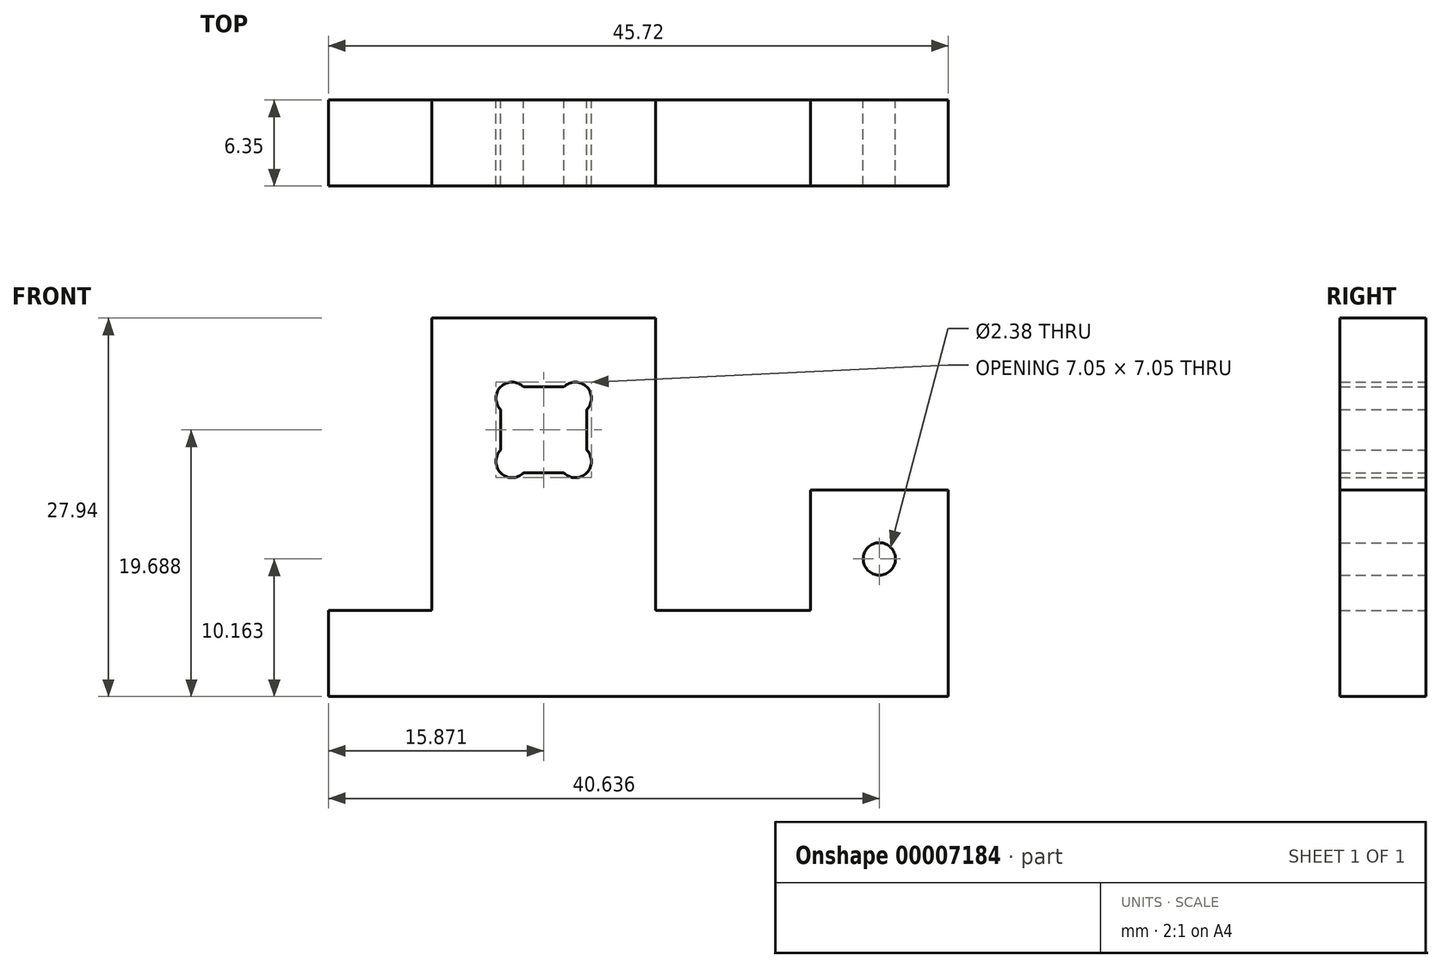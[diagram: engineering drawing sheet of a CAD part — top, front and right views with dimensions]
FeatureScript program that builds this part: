
annotation { "Feature Type Name" : "Feature", "Feature Type Description" : "" }
export const myFeature = defineFeature(function(context is Context, id is Id, definition is map)
    precondition{}
    {
        {
            var Q0;
            Q0=qCreatedBy(makeId("Front.planeOp"),FACE);
            var sketch = newSketch(context, id + "F0", { "sketchPlane" : qUnion([Q0])});
            skLineSegment(sketch, "E0", {"start": v(-37.65, 9.84) * mm, "end": v(-37.65, -11.75) * mm});
            skLineSegment(sketch, "E1", {"start": v(-37.65, -18.1) * mm, "end": v(0.45, -18.1) * mm});
            skLineSegment(sketch, "E2", {"start": v(0.45, -2.86) * mm, "end": v(-9.71, -2.86) * mm});
            skLineSegment(sketch, "E3", {"start": v(-9.71, -2.86) * mm, "end": v(-9.71, -11.75) * mm});
            skLineSegment(sketch, "E4", {"start": v(-9.71, -11.75) * mm, "end": v(-21.14, -11.75) * mm});
            skLineSegment(sketch, "E5", {"start": v(-21.14, -11.75) * mm, "end": v(-21.14, 9.84) * mm});
            skLineSegment(sketch, "E6", {"start": v(-21.14, 9.84) * mm, "end": v(-37.65, 9.84) * mm});
            skLineSegment(sketch, "E7.bottom", {"start": v(-30.9, 4.76) * mm, "end": v(-27.9, 4.76) * mm});
            skLineSegment(sketch, "E7.top", {"start": v(-30.9, -1.59) * mm, "end": v(-27.9, -1.59) * mm});
            skLineSegment(sketch, "E7.left", {"start": v(-32.57, 3.08) * mm, "end": v(-32.57, 0.1) * mm});
            skLineSegment(sketch, "E7.right", {"start": v(-26.22, 3.08) * mm, "end": v(-26.22, 0.1) * mm});
            skPoint(sketch, "E8", {"position": v(-4.63, -2.86) * mm});
            skCircle(sketch, "E9", {"center": v(-4.63, -7.94) * mm, "radius": 1.2 * mm});
            skLineSegment(sketch, "E10", {"start": v(0.45, -2.86) * mm, "end": v(0.45, -18.1) * mm});
            skLineSegment(sketch, "E11.bottom", {"start": v(-37.65, -11.75) * mm, "end": v(-45.27, -11.75) * mm});
            skLineSegment(sketch, "E11.top", {"start": v(-37.65, -18.1) * mm, "end": v(-45.27, -18.1) * mm});
            skLineSegment(sketch, "E11.right", {"start": v(-45.27, -11.75) * mm, "end": v(-45.27, -18.1) * mm});
            skLineSegment(sketch, "E12", {"start": v(-32.57, 4.76) * mm, "end": v(-26.22, -1.59) * mm, "construction": true});
            skLineSegment(sketch, "E13", {"start": v(-26.22, 4.76) * mm, "end": v(-32.57, -1.59) * mm, "construction": true});
            skArc(sketch, "E14", {"start": v(-30.9, 4.76) * mm, "mid": v(-32.57, 4.76) * mm, "end": v(-32.57, 3.08) * mm});
            skArc(sketch, "E15", {"start": v(-26.22, 3.08) * mm, "mid": v(-26.22, 4.76) * mm, "end": v(-27.9, 4.76) * mm});
            skArc(sketch, "E16", {"start": v(-27.9, -1.59) * mm, "mid": v(-26.22, -1.59) * mm, "end": v(-26.22, 0.1) * mm});
            skArc(sketch, "E17", {"start": v(-32.57, 0.1) * mm, "mid": v(-32.57, -1.59) * mm, "end": v(-30.9, -1.59) * mm});
            skSolve(sketch);
        }
        {
            var Q0;
            Q0=makeQuery(id+"F0.imprint","IMPRINT",FACE,{"disambiguationData":[TD([[makeQuery(id+"F0.imprint","IMPRINT",EDGE,{"derivedFrom":sQuery(id+"F0.wireOp",EDGE,"E0")}),1.0]])]});
            extrude(context, id + "F1", {"entities" : qUnion([Q0]), "depth" : 6.35 * mm});
        }
    });
